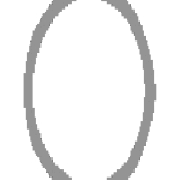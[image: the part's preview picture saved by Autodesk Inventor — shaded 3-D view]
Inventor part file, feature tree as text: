
AUTODESK INVENTOR PART (.ipt)
format: ipt  version: 2021 (Build 250183000, 183)  size: 114,688 bytes
history: native  units: in
note: dims shown in document units (in); Inventor stores cm internally (conversion verified against a paired STEP export)
features: other x4, sketch x3, plane x1
ambient origin geometry x8: Origin, YZ Plane, XZ Plane, XY Plane, X Axis, Y Axis, Z Axis, Center Point
bodies: Solid1 (feature_tree), Body (feature_tree)
feature tree (8):
  other  "Driven Length"
  other  "Frame Generator"
  other  "Start Plane"
  other  "End Plane"
  sketch  "Sketch"  dims[d2=6.7082in d4=-0.0in d5=6.7082in d6=0.12in d7=0.0in d8=90.0deg d9=6.7082in]
  sketch  "Sketch2"  dims[d0=1.0in]
  plane  "Work Plane3"
  sketch  "Sketch3"  dims[d1=0.065in]
